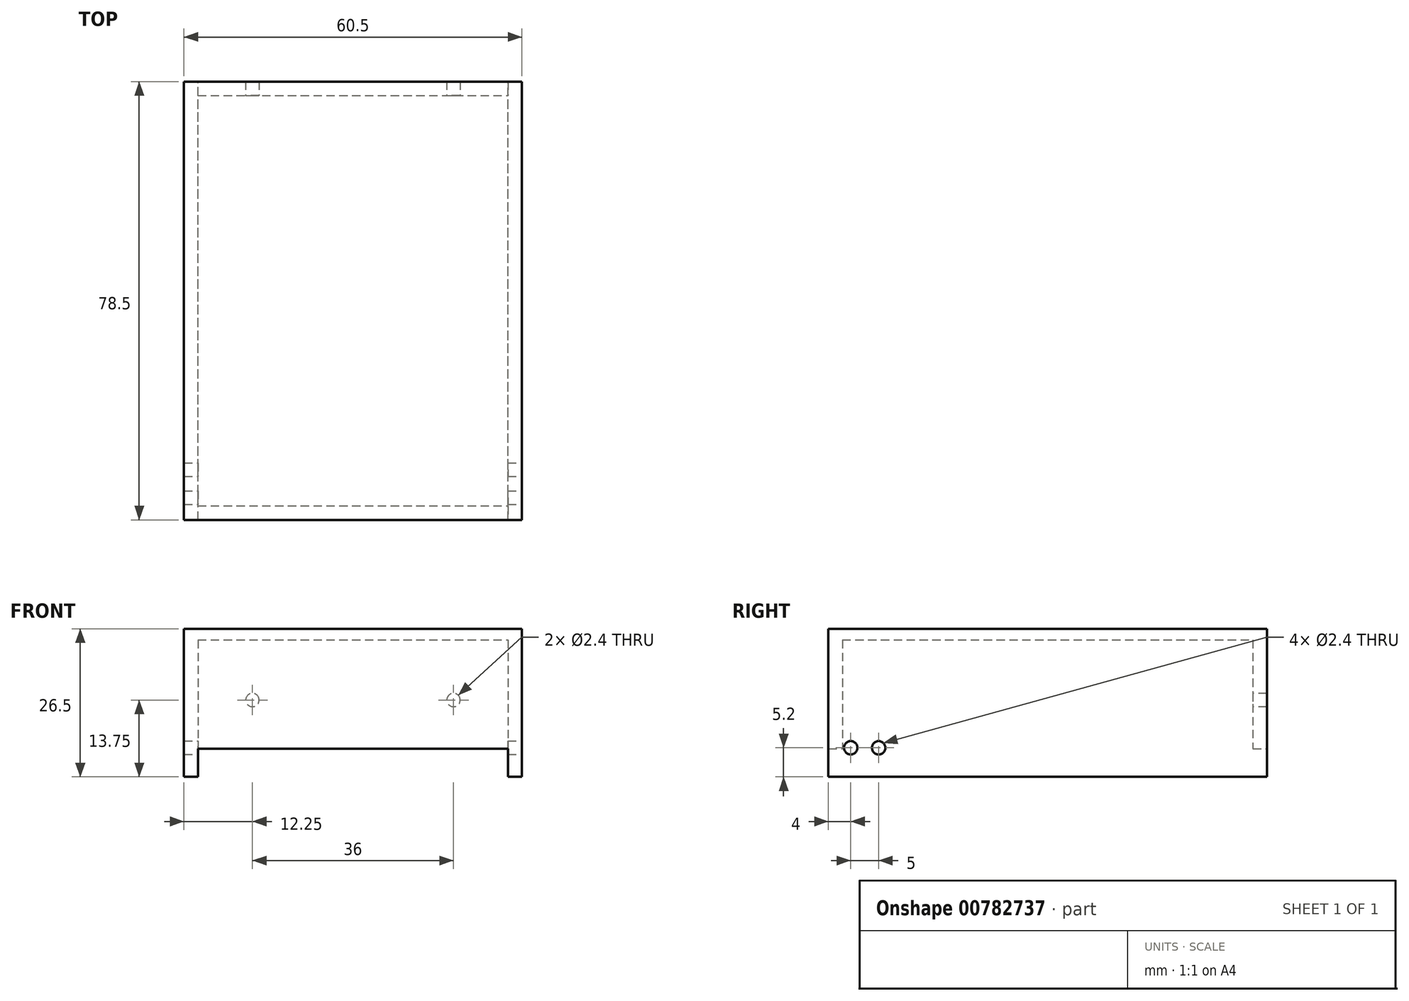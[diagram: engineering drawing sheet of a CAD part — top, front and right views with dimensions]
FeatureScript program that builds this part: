
annotation { "Feature Type Name" : "Feature", "Feature Type Description" : "" }
export const myFeature = defineFeature(function(context is Context, id is Id, definition is map)
    precondition{}
    {
        {
            var Q0;
            Q0=qCreatedBy(makeId("Top.planeOp"),FACE);
            var sketch = newSketch(context, id + "F0", { "sketchPlane" : qUnion([Q0])});
            skLineSegment(sketch, "E0.bottom", {"start": v(0, 0) * mm, "end": v(55.5, 0) * mm});
            skLineSegment(sketch, "E0.top", {"start": v(0, 73.5) * mm, "end": v(55.5, 73.5) * mm});
            skLineSegment(sketch, "E0.left", {"start": v(0, 0) * mm, "end": v(0, 73.5) * mm});
            skLineSegment(sketch, "E0.right", {"start": v(55.5, 0) * mm, "end": v(55.5, 73.5) * mm});
            skSolve(sketch);
        }
        {
            var Q0;
            Q0=qCreatedBy(makeId("Top.planeOp"),FACE);
            var sketch = newSketch(context, id + "F1", { "sketchPlane" : qUnion([Q0])});
            skLineSegment(sketch, "E1.bottom", {"start": v(-2.5, 76) * mm, "end": v(58, 76) * mm});
            skLineSegment(sketch, "E1.top", {"start": v(-2.5, -2.5) * mm, "end": v(58, -2.5) * mm});
            skLineSegment(sketch, "E1.left", {"start": v(-2.5, 76) * mm, "end": v(-2.5, -2.5) * mm});
            skLineSegment(sketch, "E1.right", {"start": v(58, 76) * mm, "end": v(58, -2.5) * mm});
            skSolve(sketch);
        }
        {
            var Q0;
            Q0=qSketchRegion(id+"F1",true);
            extrude(context, id + "F2", {"entities" : qUnion([Q0]), "depth" : 21.5 * mm, "offsetDistance" : 25 * mm});
        }
        {
            var Q0;
            Q0=qSketchRegion(id+"F0",true);
            extrude(context, id + "F3", {"entities" : qUnion([Q0]), "operationType" : NewBodyOperationType.REMOVE, "depth" : 19.5 * mm, "offsetDistance" : 25 * mm});
        }
        {
            var Q0;
            Q0=makeQuery(id+"F2.opExtrude","SWEPT_FACE",FACE,{"disambiguationData":[OSD([sQuery(id+"F1.wireOp",EDGE,"E1.right")])]});
            var sketch = newSketch(context, id + "F4", { "sketchPlane" : qUnion([Q0])});
            skLineSegment(sketch, "E2.bottom", {"start": v(-2.5, 0) * mm, "end": v(76, 0) * mm});
            skLineSegment(sketch, "E2.top", {"start": v(-2.5, -5) * mm, "end": v(76, -5) * mm});
            skLineSegment(sketch, "E2.left", {"start": v(-2.5, 0) * mm, "end": v(-2.5, -5) * mm});
            skLineSegment(sketch, "E2.right", {"start": v(76, 0) * mm, "end": v(76, -5) * mm});
            skSolve(sketch);
        }
        {
            var Q0;
            Q0=makeQuery(id+"F4.imprint","IMPRINT",FACE,{"disambiguationData":[TD([[makeQuery(id+"F4.imprint","IMPRINT",EDGE,{"derivedFrom":sQuery(id+"F4.wireOp",EDGE,"E2.bottom")}),1.0]])]});
            var Q1;
            Q1=makeQuery(id+"F3.boolean.opBoolean","COPY",FACE,{"derivedFrom":makeQuery(id+"F3.opExtrude","SWEPT_FACE",FACE,{"disambiguationData":[OSD([sQuery(id+"F0.wireOp",EDGE,"E0.right")])]})});
            extrude(context, id + "F5", {"entities" : qUnion([Q0]), "operationType" : NewBodyOperationType.ADD, "endBound" : BoundingType.UP_TO_SURFACE, "oppositeDirection" : true, "depth" : 25 * mm, "endBoundEntityFace" : qUnion([Q1]), "offsetDistance" : 25 * mm});
        }
        {
            var Q0;
            Q0=makeQuery(id+"F5.boolean.opBoolean","MERGE",FACE,{"derivedFrom":[makeQuery(id+"F2.opExtrude","SWEPT_FACE",FACE,{"disambiguationData":[OSD([sQuery(id+"F1.wireOp",EDGE,"E1.right")])]}),makeQuery(id+"F5.opExtrude","CAP_FACE",FACE,{"disambiguationData":[OSD([sQuery(id+"F4.wireOp",EDGE,"E2.bottom"),sQuery(id+"F4.wireOp",EDGE,"E2.top"),sQuery(id+"F4.wireOp",EDGE,"E2.left"),sQuery(id+"F4.wireOp",EDGE,"E2.right")])],"isStart":true})]});
            var sketch = newSketch(context, id + "F6", { "sketchPlane" : qUnion([Q0])});
            skCircle(sketch, "E3", {"center": v(1.5, 0.2) * mm, "radius": 1.2 * mm});
            skCircle(sketch, "E4.1.0.0", {"center": v(6.5, 0.2) * mm, "radius": 1.2 * mm});
            skLineSegment(sketch, "E4.direction1", {"start": v(1.5, 0.2) * mm, "end": v(6.5, 0.2) * mm, "construction": true});
            skSolve(sketch);
        }
        {
            var Q0;
            Q0=qSketchRegion(id+"F6",true);
            extrude(context, id + "F7", {"entities" : qUnion([Q0]), "operationType" : NewBodyOperationType.REMOVE, "oppositeDirection" : true, "depth" : 25 * mm, "offsetDistance" : 25 * mm});
        }
        {
            var Q0;
            Q0=makeQuery(id+"F2.opExtrude","SWEPT_FACE",FACE,{"disambiguationData":[OSD([sQuery(id+"F1.wireOp",EDGE,"E1.left")])]});
            var sketch = newSketch(context, id + "F8", { "sketchPlane" : qUnion([Q0])});
            skLineSegment(sketch, "E5.bottom", {"start": v(-76, 0) * mm, "end": v(2.5, 0) * mm});
            skLineSegment(sketch, "E5.top", {"start": v(-76, -5) * mm, "end": v(2.5, -5) * mm});
            skLineSegment(sketch, "E5.left", {"start": v(-76, 0) * mm, "end": v(-76, -5) * mm});
            skLineSegment(sketch, "E5.right", {"start": v(2.5, 0) * mm, "end": v(2.5, -5) * mm});
            skSolve(sketch);
        }
        {
            var Q0;
            Q0=qSketchRegion(id+"F8",true);
            var Q1;
            Q1=makeQuery(id+"F3.boolean.opBoolean","COPY",FACE,{"derivedFrom":makeQuery(id+"F3.opExtrude","SWEPT_FACE",FACE,{"disambiguationData":[OSD([sQuery(id+"F0.wireOp",EDGE,"E0.left")])]})});
            var Q2;
            Q2=makeQuery(id+"F2.opExtrude","SWEPT_BODY",BODY,{"disambiguationData":[OSD([sQuery(id+"F1.wireOp",EDGE,"E1.bottom"),sQuery(id+"F1.wireOp",EDGE,"E1.top"),sQuery(id+"F1.wireOp",EDGE,"E1.left"),sQuery(id+"F1.wireOp",EDGE,"E1.right")])]});
            extrude(context, id + "F9", {"entities" : qUnion([Q0]), "operationType" : NewBodyOperationType.ADD, "endBound" : BoundingType.UP_TO_SURFACE, "oppositeDirection" : true, "depth" : 25 * mm, "endBoundEntityFace" : qUnion([Q1]), "endBoundEntityBody" : qUnion([Q2]), "offsetDistance" : 25 * mm});
        }
        {
            var Q0;
            Q0=qCreatedBy(makeId("Right.planeOp"),FACE);
            var sketch = newSketch(context, id + "F10", { "sketchPlane" : qUnion([Q0])});
            skCircle(sketch, "E6", {"center": v(1.5, 0.2) * mm, "radius": 1.2 * mm});
            skCircle(sketch, "E7", {"center": v(6.5, 0.2) * mm, "radius": 1.2 * mm});
            skSolve(sketch);
        }
        {
            var Q0;
            Q0=qSketchRegion(id+"F10",true);
            extrude(context, id + "F11", {"entities" : qUnion([Q0]), "operationType" : NewBodyOperationType.REMOVE, "oppositeDirection" : true, "depth" : 25 * mm, "offsetDistance" : 25 * mm});
        }
        {
            var Q0;
            Q0=makeQuery(id+"F9.boolean.opBoolean","MERGE",FACE,{"derivedFrom":[makeQuery(id+"F5.boolean.opBoolean","MERGE",FACE,{"derivedFrom":[makeQuery(id+"F2.opExtrude","SWEPT_FACE",FACE,{"disambiguationData":[OSD([sQuery(id+"F1.wireOp",EDGE,"E1.top")])]}),makeQuery(id+"F5.opExtrude","SWEPT_FACE",FACE,{"disambiguationData":[OSD([sQuery(id+"F4.wireOp",EDGE,"E2.left")])]})]}),makeQuery(id+"F9.opExtrude","SWEPT_FACE",FACE,{"disambiguationData":[OSD([sQuery(id+"F8.wireOp",EDGE,"E5.right")])]})]});
            var sketch = newSketch(context, id + "F12", { "sketchPlane" : qUnion([Q0])});
            skCircle(sketch, "E8", {"center": v(9.75, 8.75) * mm, "radius": 1.2 * mm});
            skLineSegment(sketch, "E9", {"start": v(27.75, 21.5) * mm, "end": v(27.75, 0) * mm, "construction": true});
            skCircle(sketch, "E10.MirrorC", {"center": v(45.75, 8.75) * mm, "radius": 1.2 * mm});
            skSolve(sketch);
        }
        {
            var Q0;
            Q0=qSketchRegion(id+"F12",true);
            extrude(context, id + "F13", {"entities" : qUnion([Q0]), "operationType" : NewBodyOperationType.REMOVE, "oppositeDirection" : true, "depth" : 80 * mm, "offsetDistance" : 25 * mm});
        }
        {
            var Q0;
            Q0=makeQuery(id+"F9.boolean.opBoolean","MERGE",FACE,{"derivedFrom":[makeQuery(id+"F5.boolean.opBoolean","MERGE",FACE,{"derivedFrom":[makeQuery(id+"F2.opExtrude","SWEPT_FACE",FACE,{"disambiguationData":[OSD([sQuery(id+"F1.wireOp",EDGE,"E1.top")])]}),makeQuery(id+"F5.opExtrude","SWEPT_FACE",FACE,{"disambiguationData":[OSD([sQuery(id+"F4.wireOp",EDGE,"E2.left")])]})]}),makeQuery(id+"F9.opExtrude","SWEPT_FACE",FACE,{"disambiguationData":[OSD([sQuery(id+"F8.wireOp",EDGE,"E5.right")])]})]});
            var sketch = newSketch(context, id + "F14", { "sketchPlane" : qUnion([Q0])});
            skLineSegment(sketch, "E11.bottom", {"start": v(5.06, 12.2) * mm, "end": v(49.15, 12.2) * mm});
            skLineSegment(sketch, "E11.top", {"start": v(5.06, 4.75) * mm, "end": v(49.15, 4.75) * mm});
            skLineSegment(sketch, "E11.left", {"start": v(5.06, 12.2) * mm, "end": v(5.06, 4.75) * mm});
            skLineSegment(sketch, "E11.right", {"start": v(49.15, 12.2) * mm, "end": v(49.15, 4.75) * mm});
            skSolve(sketch);
        }
        {
            var Q0;
            Q0=qSketchRegion(id+"F14",true);
            var Q1;
            Q1=makeQuery(id+"F3.boolean.opBoolean","COPY",FACE,{"derivedFrom":makeQuery(id+"F3.opExtrude","SWEPT_FACE",FACE,{"disambiguationData":[OSD([sQuery(id+"F0.wireOp",EDGE,"E0.bottom")])]})});
            extrude(context, id + "F15", {"entities" : qUnion([Q0]), "operationType" : NewBodyOperationType.ADD, "endBound" : BoundingType.UP_TO_SURFACE, "oppositeDirection" : true, "depth" : 25 * mm, "endBoundEntityFace" : qUnion([Q1]), "offsetDistance" : 25 * mm});
        }
    });
